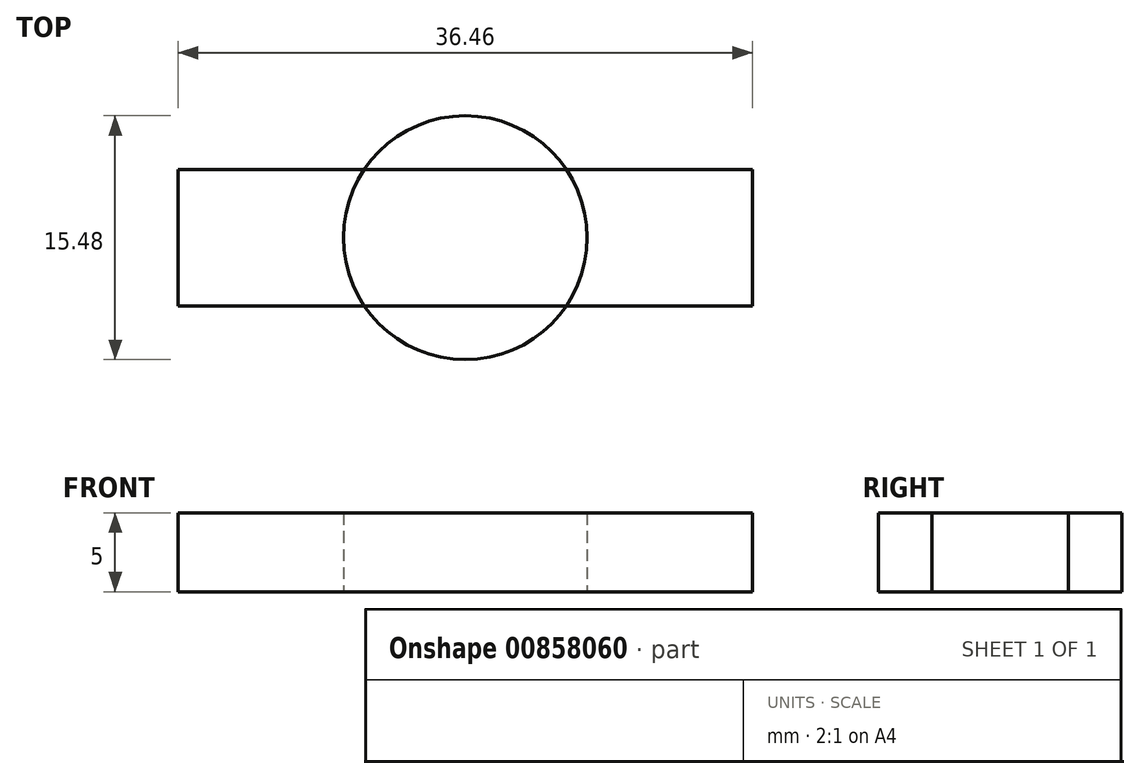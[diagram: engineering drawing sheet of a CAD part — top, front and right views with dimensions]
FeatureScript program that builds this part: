
annotation { "Feature Type Name" : "Feature", "Feature Type Description" : "" }
export const myFeature = defineFeature(function(context is Context, id is Id, definition is map)
    precondition{}
    {
        {
            var Q0;
            Q0=qCreatedBy(makeId("Top.planeOp"),FACE);
            var sketch = newSketch(context, id + "F0", { "sketchPlane" : qUnion([Q0])});
            skLineSegment(sketch, "E0.bottom", {"start": v(-18.23, -4.33) * mm, "end": v(18.23, -4.33) * mm});
            skLineSegment(sketch, "E0.top", {"start": v(-18.23, 4.33) * mm, "end": v(18.23, 4.33) * mm});
            skLineSegment(sketch, "E0.left", {"start": v(-18.23, -4.33) * mm, "end": v(-18.23, 4.33) * mm});
            skLineSegment(sketch, "E0.right", {"start": v(18.23, -4.33) * mm, "end": v(18.23, 4.33) * mm});
            skPoint(sketch, "E0.middle", {"position": v(0, 0) * mm});
            skSolve(sketch);
        }
        {
            var Q0;
            Q0=qCreatedBy(makeId("Top.planeOp"),FACE);
            var sketch = newSketch(context, id + "F1", { "sketchPlane" : qUnion([Q0])});
            skCircle(sketch, "E1", {"center": v(0, 0) * mm, "radius": 7.74 * mm});
            skSolve(sketch);
        }
        {
            var Q0;
            Q0=makeQuery(id+"F0.imprint","IMPRINT",FACE,{"disambiguationData":[TD([[makeQuery(id+"F0.imprint","IMPRINT",EDGE,{"derivedFrom":sQuery(id+"F0.wireOp",EDGE,"E0.bottom")}),1.0]])]});
            var Q1;
            Q1=makeQuery(id+"F1.imprint","IMPRINT",FACE,{"disambiguationData":[TD([[makeQuery(id+"F1.imprint","IMPRINT",EDGE,{"derivedFrom":sQuery(id+"F1.wireOp",EDGE,"E1")}),1.0]])]});
            extrude(context, id + "F2", {"entities" : qUnion([Q0, Q1]), "depth" : 5 * mm, "offsetDistance" : 25 * mm});
        }
    });
